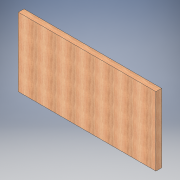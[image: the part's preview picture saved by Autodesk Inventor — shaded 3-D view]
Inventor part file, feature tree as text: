
AUTODESK INVENTOR PART (.ipt)
format: ipt  version: 2017 (Build 210142000, 142)  size: 112,640 bytes
history: native  units: in
note: dims shown in document units (in); Inventor stores cm internally (conversion verified against a paired STEP export)
features: extrude x1, sketch x1
ambient origin geometry x8: Origin, YZ Plane, XZ Plane, XY Plane, X Axis, Y Axis, Z Axis, Center Point
bodies: Body1 (feature_tree)
feature tree (2):
  extrude  "Extrusion2"  Depth=3.0in
  sketch  "Sketch2"  dims[d4=72.0in d5=3.0in d6=36.0in d7=0.0in]
